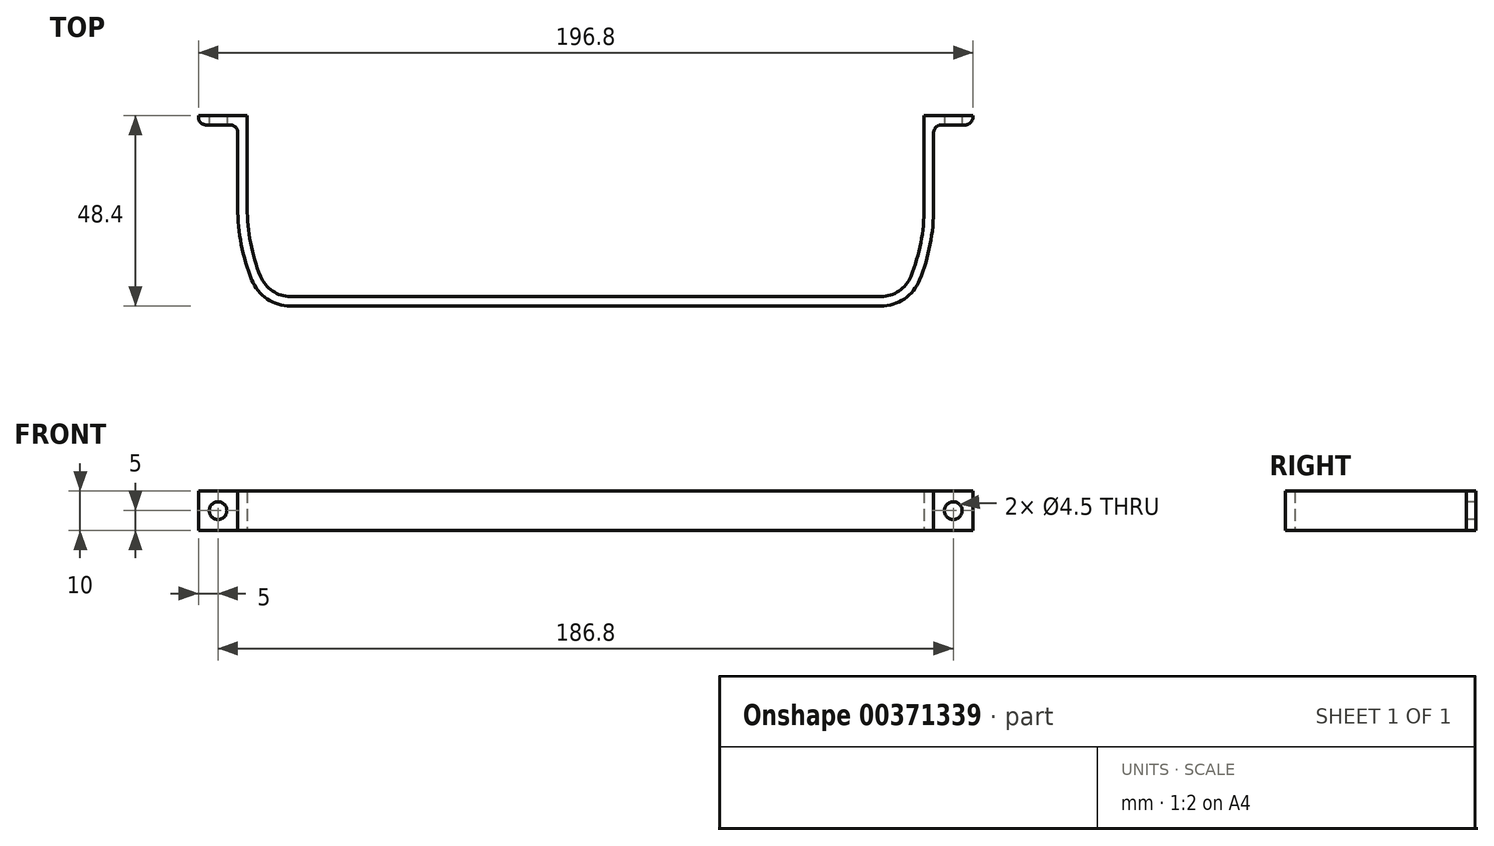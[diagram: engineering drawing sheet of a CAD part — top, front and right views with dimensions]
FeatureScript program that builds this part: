
annotation { "Feature Type Name" : "Feature", "Feature Type Description" : "" }
export const myFeature = defineFeature(function(context is Context, id is Id, definition is map)
    precondition{}
    {
        {
            var Q0;
            Q0=qCreatedBy(makeId("Top.planeOp"),FACE);
            var sketch = newSketch(context, id + "F0", { "sketchPlane" : qUnion([Q0])});
            skLineSegment(sketch, "E0", {"start": v(0, 0) * mm, "end": v(75, 0) * mm});
            skLineSegment(sketch, "E1", {"start": v(0, 0) * mm, "end": v(0, 2.4) * mm});
            skLineSegment(sketch, "E2", {"start": v(0, 2.4) * mm, "end": v(75, 2.4) * mm});
            skArc(sketch, "E3", {"start": v(75, 0) * mm, "mid": v(80.94, 1.82) * mm, "end": v(84.85, 6.64) * mm});
            skArc(sketch, "E4", {"start": v(84.85, 6.64) * mm, "mid": v(87.5, 15.6) * mm, "end": v(88.4, 24.9) * mm});
            skLineSegment(sketch, "E5", {"start": v(88.4, 24.9) * mm, "end": v(88.4, 46) * mm});
            skLineSegment(sketch, "E6", {"start": v(88.4, 46) * mm, "end": v(98.4, 46) * mm});
            skLineSegment(sketch, "E7", {"start": v(98.4, 46) * mm, "end": v(98.4, 48.4) * mm});
            skLineSegment(sketch, "E8", {"start": v(98.4, 48.4) * mm, "end": v(86, 48.4) * mm});
            skLineSegment(sketch, "E9", {"start": v(86, 48.4) * mm, "end": v(86, 24.9) * mm});
            skArc(sketch, "E10", {"start": v(75, 2.4) * mm, "mid": v(79.6, 3.8) * mm, "end": v(82.63, 7.54) * mm});
            skArc(sketch, "E11", {"start": v(82.63, 7.54) * mm, "mid": v(85.15, 16.06) * mm, "end": v(86, 24.9) * mm});
            skPoint(sketch, "E12", {"position": v(0, 52.33) * mm});
            skLineSegment(sketch, "E13", {"start": v(39.67, 24.9) * mm, "end": v(84.85, 6.64) * mm, "construction": true});
            skLineSegment(sketch, "E14", {"start": v(39.67, 24.9) * mm, "end": v(88.4, 24.9) * mm, "construction": true});
            skSolve(sketch);
        }
        {
            var Q0;
            Q0 = qSketchRegion(id + "F0", true);
            extrude(context, id + "F1", {"entities" : qUnion([Q0]), "endBound" : BoundingType.SYMMETRIC, "depth" : 10 * mm});
        }
        {
            var Q0;
            Q0=makeQuery(id+"F1.opExtrude","SWEPT_FACE",FACE,{"disambiguationData":[OSD([sQuery(id+"F0.wireOp",EDGE,"E6")])]});
            var sketch = newSketch(context, id + "F2", { "sketchPlane" : qUnion([Q0])});
            skPoint(sketch, "E15", {"position": v(93.4, 0) * mm});
            skPoint(sketch, "E15.positionSnap0", {"position": v(93.4, 5) * mm});
            skSolve(sketch);
        }
        {
            var Q0;
            Q0=sQuery(id+"F2.wireOp",VERTEX,"E15");
            var Q1;
            Q1=makeQuery(id+"F1.opExtrude","SWEPT_BODY",BODY,{"disambiguationData":[OSD([sQuery(id+"F0.wireOp",EDGE,"E0"),sQuery(id+"F0.wireOp",EDGE,"E1"),sQuery(id+"F0.wireOp",EDGE,"E2"),sQuery(id+"F0.wireOp",EDGE,"E3"),sQuery(id+"F0.wireOp",EDGE,"E4"),sQuery(id+"F0.wireOp",EDGE,"E5"),sQuery(id+"F0.wireOp",EDGE,"E6"),sQuery(id+"F0.wireOp",EDGE,"E7"),sQuery(id+"F0.wireOp",EDGE,"E8"),sQuery(id+"F0.wireOp",EDGE,"E9"),sQuery(id+"F0.wireOp",EDGE,"E10"),sQuery(id+"F0.wireOp",EDGE,"E11")])]});
            hole(context, id + "F3", {"style" : HoleStyle.SIMPLE, "endStyle" : HoleEndStyle.THROUGH, "standardTappedOrClearance" : lookupTablePath({ "standard" : "ANSI", "fit" : "Normal (ASME)", "size" : "#8", "type" : "Clearance" }), "standardBlindInLast" : lookupTablePath({ "fit" : "Free", "standard" : "ANSI", "size" : "#8", "type" : "Clearance" }), "holeDiameter" : 4.5 * mm, "isTappedThrough" : true, "tappedDepth" : 12 * mm, "tapClearance" : 3, "locations" : qUnion([Q0]), "scope" : qUnion([Q1])});
        }
        {
            var Q0;
            Q0=makeQuery(id+"F1.opExtrude","SWEPT_EDGE",EDGE,{"disambiguationData":[OSD([sQuery(id+"F0.wireOp",EDGE,"E5"),sQuery(id+"F0.wireOp",EDGE,"E6")])]});
            var Q1;
            Q1=makeQuery(id+"F1.opExtrude","SWEPT_EDGE",EDGE,{"disambiguationData":[OSD([sQuery(id+"F0.wireOp",EDGE,"E6"),sQuery(id+"F0.wireOp",EDGE,"E7")])]});
            fillet(context, id + "F4", {"entities" : qUnion([Q0, Q1]), "radius" : 2 * mm, "tangentPropagation" : true, "allowEdgeOverflow" : false});
        }
        {
            var Q0;
            Q0=makeQuery(id+"F1.opExtrude","SWEPT_BODY",BODY,{"disambiguationData":[OSD([sQuery(id+"F0.wireOp",EDGE,"E0"),sQuery(id+"F0.wireOp",EDGE,"E1"),sQuery(id+"F0.wireOp",EDGE,"E2"),sQuery(id+"F0.wireOp",EDGE,"E3"),sQuery(id+"F0.wireOp",EDGE,"E4"),sQuery(id+"F0.wireOp",EDGE,"E5"),sQuery(id+"F0.wireOp",EDGE,"E6"),sQuery(id+"F0.wireOp",EDGE,"E7"),sQuery(id+"F0.wireOp",EDGE,"E8"),sQuery(id+"F0.wireOp",EDGE,"E9"),sQuery(id+"F0.wireOp",EDGE,"E10"),sQuery(id+"F0.wireOp",EDGE,"E11")])]});
            var Q1;
            Q1=makeQuery(id+"F1.opExtrude","SWEPT_FACE",FACE,{"disambiguationData":[OSD([sQuery(id+"F0.wireOp",EDGE,"E1")])]});
            mirror(context, id + "F5", {"operationType" : NewBodyOperationType.ADD, "entities" : qUnion([Q0]), "mirrorPlane" : qUnion([Q1])});
        }
    });
